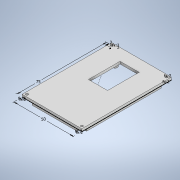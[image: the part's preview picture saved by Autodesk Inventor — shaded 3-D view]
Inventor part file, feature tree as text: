
AUTODESK INVENTOR PART (.ipt)
format: ipt  version: 2020.2 (Build 242310000, 310)  size: 190,976 bytes
history: native  units: mm
features: sketch x4, extrude x4
ambient origin geometry x8: Origin, YZ Plane, XZ Plane, XY Plane, X Axis, Y Axis, Z Axis, Center Point
bodies: Solid1 (feature_tree)
feature tree (8):
  sketch  "Sketch1"  dims[d0=75.0mm d1=50.0mm]
  extrude  "Extrusion1"  Depth=50.0mm
  extrude  "Extrusion4"  Depth=2.0mm
  extrude  "Extrusion5"  Depth=2.0mm
  extrude  "Extrusion6"  Depth=2.0mm
  sketch  "Sketch4"  dims[d4=2.0mm d5=0.0mm d17=2.0mm]
  sketch  "Sketch5"  dims[d18=2.0mm d21=2.0mm]
  sketch  "Sketch6"  dims[d22=2.0mm d23=2.0mm d25=2.0mm d26=2.0mm d27=2.0mm d28=2.0mm d29=2.2mm d30=2.2mm d32=4.0mm d33=4.0mm d34=0.0mm d35=2.0mm d36=23.25mm d37=23.0mm d38=2.0mm d39=4.0mm d40=2.0mm d41=0.0mm d42=16.0mm d43=26.5mm d45=1.5mm d46=10.0mm d47=0.0mm]
